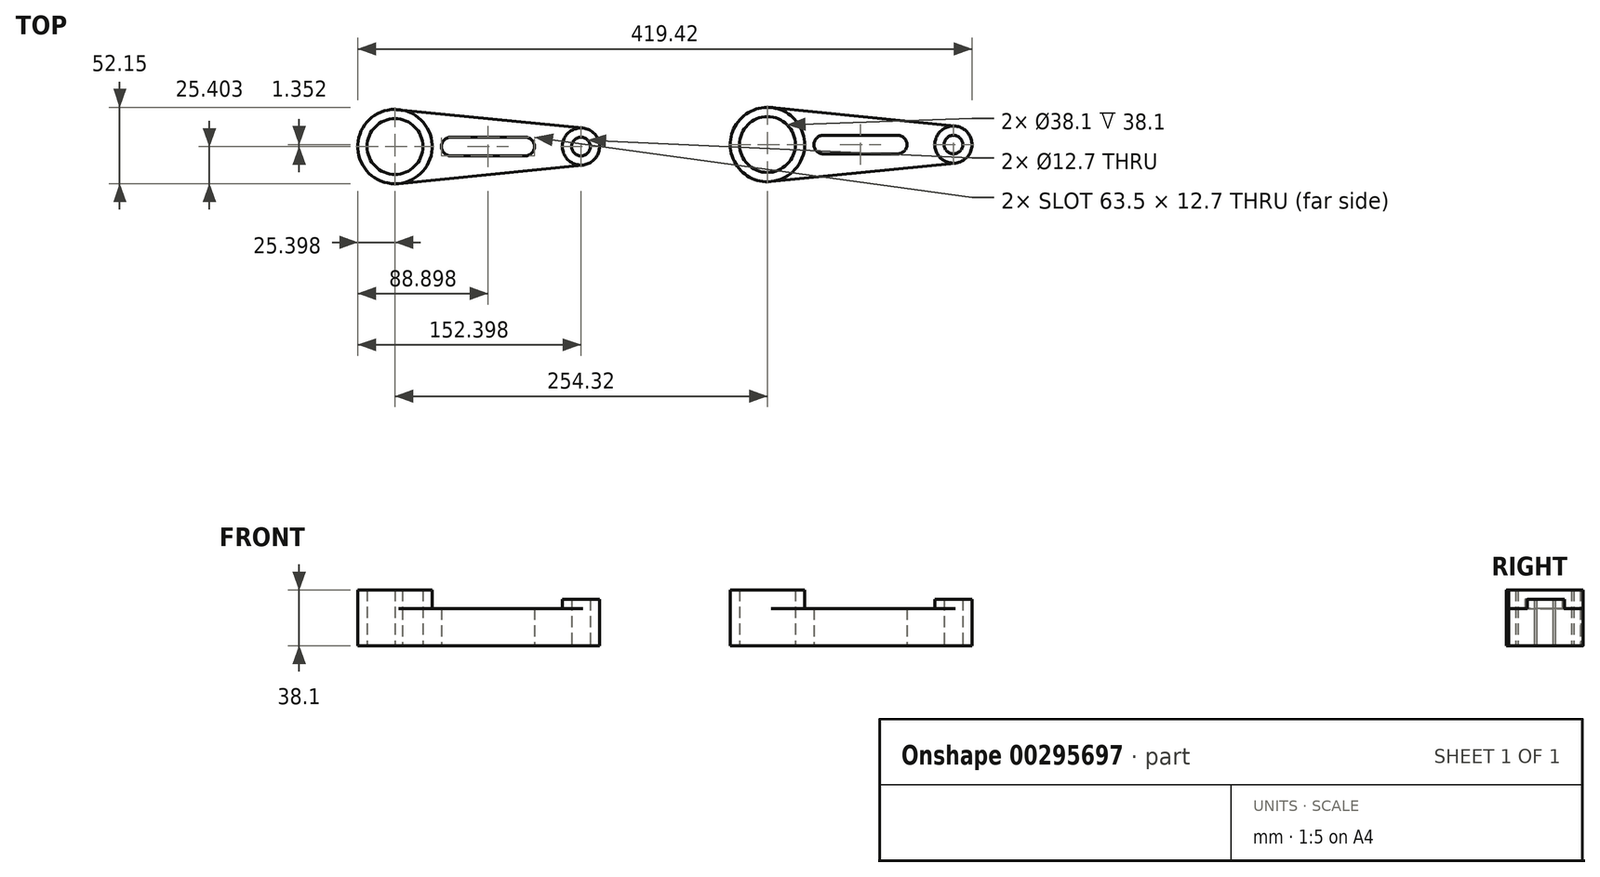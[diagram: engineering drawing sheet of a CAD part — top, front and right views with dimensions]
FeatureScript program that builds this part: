
annotation { "Feature Type Name" : "Feature", "Feature Type Description" : "" }
export const myFeature = defineFeature(function(context is Context, id is Id, definition is map)
    precondition{}
    {
        {
            var Q0;
            Q0=qCreatedBy(makeId("Top.planeOp"),FACE);
            var sketch = newSketch(context, id + "F0", { "sketchPlane" : qUnion([Q0])});
            skCircle(sketch, "E0", {"center": v(-79.2, -1.87) * mm, "radius": 19.05 * mm});
            skCircle(sketch, "E1", {"center": v(-79.2, -1.87) * mm, "radius": 25.4 * mm});
            skArc(sketch, "E2", {"start": v(-41.1, 4.48) * mm, "mid": v(-47.45, -1.87) * mm, "end": v(-41.1, -8.22) * mm});
            skArc(sketch, "E3", {"start": v(9.7, -8.22) * mm, "mid": v(16.05, -1.87) * mm, "end": v(9.7, 4.48) * mm});
            skCircle(sketch, "E4", {"center": v(47.8, -1.87) * mm, "radius": 6.35 * mm});
            skCircle(sketch, "E5", {"center": v(47.8, -1.87) * mm, "radius": 12.7 * mm});
            skLineSegment(sketch, "E6", {"start": v(-41.1, 4.48) * mm, "end": v(9.7, 4.48) * mm});
            skLineSegment(sketch, "E7", {"start": v(-41.1, -8.22) * mm, "end": v(9.7, -8.22) * mm});
            skLineSegment(sketch, "E8", {"start": v(-76.66, -27.14) * mm, "end": v(49.07, -14.5) * mm});
            skLineSegment(sketch, "E9", {"start": v(-76.66, 23.4) * mm, "end": v(49.07, 10.77) * mm});
            skCircle(sketch, "E10", {"center": v(-333.52, -3.22) * mm, "radius": 19.05 * mm});
            skCircle(sketch, "E11", {"center": v(-333.52, -3.22) * mm, "radius": 25.4 * mm});
            skArc(sketch, "E12", {"start": v(-295.42, 3.13) * mm, "mid": v(-301.77, -3.22) * mm, "end": v(-295.42, -9.57) * mm});
            skArc(sketch, "E13", {"start": v(-244.62, -9.57) * mm, "mid": v(-238.27, -3.22) * mm, "end": v(-244.62, 3.13) * mm});
            skCircle(sketch, "E14", {"center": v(-206.52, -3.22) * mm, "radius": 12.7 * mm});
            skCircle(sketch, "E15", {"center": v(-206.52, -3.22) * mm, "radius": 6.35 * mm});
            skLineSegment(sketch, "E16", {"start": v(-295.42, 3.13) * mm, "end": v(-244.62, 3.13) * mm});
            skLineSegment(sketch, "E17", {"start": v(-295.42, -9.57) * mm, "end": v(-244.62, -9.57) * mm});
            skLineSegment(sketch, "E18", {"start": v(-330.98, -28.5) * mm, "end": v(-205.25, -15.85) * mm});
            skLineSegment(sketch, "E19", {"start": v(-333.52, 22.18) * mm, "end": v(-205.26, 9.42) * mm});
            skLineSegment(sketch, "E20.MirrorCS", {"start": v(-321.05, 71.36) * mm, "end": v(-200.27, 34.2) * mm});
            skLineSegment(sketch, "E21.MirrorCS", {"start": v(-292.42, 33.35) * mm, "end": v(-242.61, 23.34) * mm});
            skLineSegment(sketch, "E22.MirrorCS", {"start": v(-289.91, 45.8) * mm, "end": v(-240.1, 35.8) * mm});
            skCircle(sketch, "E23.MirrorC", {"center": v(-204, 22.06) * mm, "radius": 12.7 * mm});
            skCircle(sketch, "E24.MirrorC", {"center": v(-204, 22.06) * mm, "radius": 6.35 * mm});
            skCircle(sketch, "E25.MirrorC", {"center": v(-328.52, 47.08) * mm, "radius": 19.05 * mm});
            skCircle(sketch, "E26.MirrorC", {"center": v(-328.52, 47.08) * mm, "radius": 25.4 * mm});
            skArc(sketch, "E27.MirrorCS", {"start": v(-292.42, 33.35) * mm, "mid": v(-297.39, 40.83) * mm, "end": v(-289.91, 45.8) * mm});
            skArc(sketch, "E28.MirrorCS", {"start": v(-240.1, 35.8) * mm, "mid": v(-235.13, 28.31) * mm, "end": v(-242.61, 23.34) * mm});
            skSolve(sketch);
        }
        {
            var Q0;
            Q0=makeQuery(id+"F0.imprint","IMPRINT",FACE,{"disambiguationData":[TD([[makeQuery(id+"F0.imprint","IMPRINT",EDGE,{"derivedFrom":sQuery(id+"F0.wireOp",EDGE,"E0")}),-1.0]])]});
            extrude(context, id + "F1", {"entities" : qUnion([Q0]), "depth" : 38.1 * mm});
        }
        {
            var Q0;
            Q0=makeQuery(id+"F0.imprint","IMPRINT",FACE,{"disambiguationData":[TD([[makeQuery(id+"F0.imprint","IMPRINT",EDGE,{"derivedFrom":sQuery(id+"F0.wireOp",EDGE,"E2")}),-1.0]])]});
            extrude(context, id + "F2", {"entities" : qUnion([Q0]), "operationType" : NewBodyOperationType.ADD, "depth" : 25.4 * mm});
        }
        {
            var Q0;
            Q0=makeQuery(id+"F0.imprint","IMPRINT",FACE,{"disambiguationData":[TD([[makeQuery(id+"F0.imprint","IMPRINT",EDGE,{"derivedFrom":sQuery(id+"F0.wireOp",EDGE,"E4")}),-1.0]])]});
            extrude(context, id + "F3", {"entities" : qUnion([Q0]), "operationType" : NewBodyOperationType.ADD, "depth" : 31.75 * mm});
        }
        {
            var Q0;
            Q0=makeQuery(id+"F0.imprint","IMPRINT",FACE,{"disambiguationData":[TD([[makeQuery(id+"F0.imprint","IMPRINT",EDGE,{"derivedFrom":sQuery(id+"F0.wireOp",EDGE,"E10")}),-1.0]])]});
            extrude(context, id + "F4", {"entities" : qUnion([Q0]), "depth" : 38.1 * mm});
        }
        {
            var Q0;
            Q0=makeQuery(id+"F0.imprint","IMPRINT",FACE,{"disambiguationData":[TD([[makeQuery(id+"F0.imprint","IMPRINT",EDGE,{"derivedFrom":sQuery(id+"F0.wireOp",EDGE,"E12")}),-1.0]])]});
            extrude(context, id + "F5", {"entities" : qUnion([Q0]), "operationType" : NewBodyOperationType.ADD, "depth" : 25.4 * mm});
        }
        {
            var Q0;
            Q0=makeQuery(id+"F0.imprint","IMPRINT",FACE,{"disambiguationData":[TD([[makeQuery(id+"F0.imprint","IMPRINT",EDGE,{"derivedFrom":sQuery(id+"F0.wireOp",EDGE,"E15")}),-1.0]])]});
            extrude(context, id + "F6", {"entities" : qUnion([Q0]), "operationType" : NewBodyOperationType.ADD, "depth" : 31.75 * mm});
        }
    });
